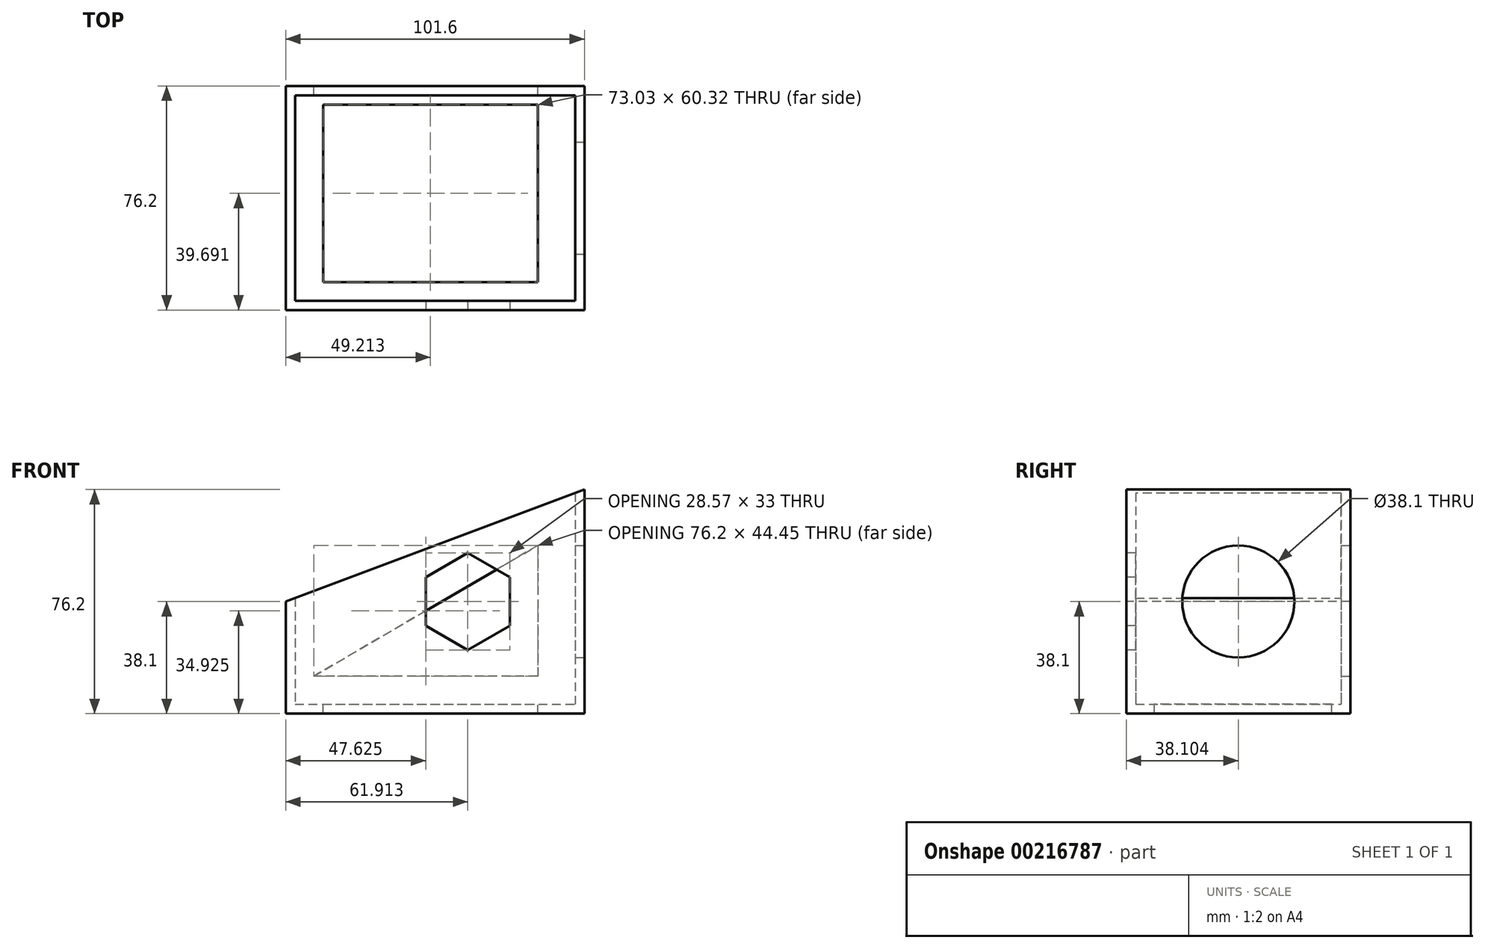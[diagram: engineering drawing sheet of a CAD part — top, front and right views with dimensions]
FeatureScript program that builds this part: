
annotation { "Feature Type Name" : "Feature", "Feature Type Description" : "" }
export const myFeature = defineFeature(function(context is Context, id is Id, definition is map)
    precondition{}
    {
        {
            var Q0;
            Q0=qCreatedBy(makeId("Top.planeOp"),FACE);
            var sketch = newSketch(context, id + "F0", { "sketchPlane" : qUnion([Q0])});
            skLineSegment(sketch, "E0.bottom", {"start": v(-48.15, -36.29) * mm, "end": v(53.45, -36.29) * mm});
            skLineSegment(sketch, "E0.top", {"start": v(-48.15, 39.91) * mm, "end": v(53.45, 39.91) * mm});
            skLineSegment(sketch, "E0.left", {"start": v(-48.15, -36.29) * mm, "end": v(-48.15, 39.91) * mm});
            skLineSegment(sketch, "E0.right", {"start": v(53.45, -36.29) * mm, "end": v(53.45, 39.91) * mm});
            skSolve(sketch);
        }
        {
            var Q0;
            Q0=makeQuery(id+"F0.imprint","IMPRINT",FACE,{"disambiguationData":[TD([[makeQuery(id+"F0.imprint","IMPRINT",EDGE,{"derivedFrom":sQuery(id+"F0.wireOp",EDGE,"E0.bottom")}),1.0]])]});
            extrude(context, id + "F1", {"entities" : qUnion([Q0]), "depth" : 3.17 * mm});
        }
        {
            var Q0;
            Q0=makeQuery(id+"F1.opExtrude","CAP_FACE",FACE,{"disambiguationData":[OSD([sQuery(id+"F0.wireOp",EDGE,"E0.bottom"),sQuery(id+"F0.wireOp",EDGE,"E0.top"),sQuery(id+"F0.wireOp",EDGE,"E0.left"),sQuery(id+"F0.wireOp",EDGE,"E0.right")])],"isStart":false});
            var sketch = newSketch(context, id + "F2", { "sketchPlane" : qUnion([Q0])});
            skLineSegment(sketch, "E1.bottom", {"start": v(-48.15, -36.29) * mm, "end": v(53.45, -36.29) * mm});
            skLineSegment(sketch, "E1.top", {"start": v(-48.15, 39.91) * mm, "end": v(53.45, 39.91) * mm});
            skLineSegment(sketch, "E1.left", {"start": v(-48.15, -36.29) * mm, "end": v(-48.15, 39.91) * mm});
            skLineSegment(sketch, "E1.right", {"start": v(53.45, -36.29) * mm, "end": v(53.45, 39.91) * mm});
            skLineSegment(sketch, "E2.0", {"start": v(50.28, 36.74) * mm, "end": v(-44.97, 36.74) * mm});
            skLineSegment(sketch, "E2.1", {"start": v(50.28, -33.11) * mm, "end": v(50.28, 36.74) * mm});
            skLineSegment(sketch, "E2.2", {"start": v(-44.97, -33.11) * mm, "end": v(50.28, -33.11) * mm});
            skLineSegment(sketch, "E2.3", {"start": v(-44.97, 36.74) * mm, "end": v(-44.97, -33.11) * mm});
            skSolve(sketch);
        }
        {
            var Q0;
            Q0 = qSketchRegion(id + "F2", true);
            extrude(context, id + "F3", {"entities" : qUnion([Q0]), "operationType" : NewBodyOperationType.ADD, "depth" : 73.02 * mm});
        }
        {
            var Q0;
            Q0=makeQuery(id+"F3.boolean.opBoolean","MERGE",FACE,{"derivedFrom":[makeQuery(id+"F1.opExtrude","SWEPT_FACE",FACE,{"disambiguationData":[OSD([sQuery(id+"F0.wireOp",EDGE,"E0.bottom")])]}),makeQuery(id+"F3.opExtrude","SWEPT_FACE",FACE,{"disambiguationData":[OSD([sQuery(id+"F2.wireOp",EDGE,"E1.bottom")])]})]});
            var sketch = newSketch(context, id + "F4", { "sketchPlane" : qUnion([Q0])});
            skLineSegment(sketch, "E3", {"start": v(-48.15, 0) * mm, "end": v(-48.15, 38.1) * mm, "construction": true});
            skLineSegment(sketch, "E4", {"start": v(-48.15, 38.1) * mm, "end": v(53.45, 76.2) * mm});
            skLineSegment(sketch, "E5", {"start": v(-48.15, 38.1) * mm, "end": v(-48.15, 76.2) * mm});
            skLineSegment(sketch, "E6", {"start": v(-48.15, 76.2) * mm, "end": v(53.45, 76.2) * mm});
            skSolve(sketch);
        }
        {
            var Q0;
            Q0 = qSketchRegion(id + "F4", true);
            extrude(context, id + "F5", {"entities" : qUnion([Q0]), "operationType" : NewBodyOperationType.REMOVE, "endBound" : BoundingType.THROUGH_ALL, "oppositeDirection" : true, "depth" : 25.4 * mm});
        }
        {
            var Q0;
            Q0=makeQuery(id+"F3.boolean.opBoolean","MERGE",FACE,{"derivedFrom":[makeQuery(id+"F1.opExtrude","SWEPT_FACE",FACE,{"disambiguationData":[OSD([sQuery(id+"F0.wireOp",EDGE,"E0.right")])]}),makeQuery(id+"F3.opExtrude","SWEPT_FACE",FACE,{"disambiguationData":[OSD([sQuery(id+"F2.wireOp",EDGE,"E1.right")])]})]});
            var sketch = newSketch(context, id + "F6", { "sketchPlane" : qUnion([Q0])});
            skCircle(sketch, "E7", {"center": v(1.81, 38.1) * mm, "radius": 19.05 * mm});
            skPoint(sketch, "E7.centerSnap0", {"position": v(39.91, 38.1) * mm});
            skPoint(sketch, "E7.centerSnap1", {"position": v(1.81, 76.2) * mm});
            skSolve(sketch);
        }
        {
            var Q0;
            Q0 = qSketchRegion(id + "F6", true);
            extrude(context, id + "F7", {"entities" : qUnion([Q0]), "operationType" : NewBodyOperationType.REMOVE, "oppositeDirection" : true, "depth" : 25.4 * mm});
        }
        {
            var Q0;
            Q0=makeQuery(id+"F1.opExtrude","CAP_FACE",FACE,{"disambiguationData":[OSD([sQuery(id+"F0.wireOp",EDGE,"E0.bottom"),sQuery(id+"F0.wireOp",EDGE,"E0.top"),sQuery(id+"F0.wireOp",EDGE,"E0.left"),sQuery(id+"F0.wireOp",EDGE,"E0.right")])],"isStart":false});
            var sketch = newSketch(context, id + "F8", { "sketchPlane" : qUnion([Q0])});
            skLineSegment(sketch, "E8.bottom", {"start": v(-35.45, 33.56) * mm, "end": v(37.58, 33.56) * mm});
            skLineSegment(sketch, "E8.top", {"start": v(-35.45, -26.76) * mm, "end": v(37.58, -26.76) * mm});
            skLineSegment(sketch, "E8.left", {"start": v(-35.45, 33.56) * mm, "end": v(-35.45, -26.76) * mm});
            skLineSegment(sketch, "E8.right", {"start": v(37.58, 33.56) * mm, "end": v(37.58, -26.76) * mm});
            skSolve(sketch);
        }
        {
            var Q0;
            Q0 = qSketchRegion(id + "F8", true);
            extrude(context, id + "F9", {"entities" : qUnion([Q0]), "operationType" : NewBodyOperationType.REMOVE, "endBound" : BoundingType.THROUGH_ALL, "oppositeDirection" : true, "depth" : 25.4 * mm});
        }
        {
            var Q0;
            Q0=makeQuery(id+"F3.boolean.opBoolean","MERGE",FACE,{"derivedFrom":[makeQuery(id+"F1.opExtrude","SWEPT_FACE",FACE,{"disambiguationData":[OSD([sQuery(id+"F0.wireOp",EDGE,"E0.bottom")])]}),makeQuery(id+"F3.opExtrude","SWEPT_FACE",FACE,{"disambiguationData":[OSD([sQuery(id+"F2.wireOp",EDGE,"E1.bottom")])]})]});
            var sketch = newSketch(context, id + "F10", { "sketchPlane" : qUnion([Q0])});
            skCircle(sketch, "E9.cCircle", {"center": v(13.76, 38.1) * mm, "radius": 14.29 * mm, "construction": true});
            skLineSegment(sketch, "E9.0", {"start": v(28.05, 46.35) * mm, "end": v(28.05, 29.85) * mm});
            skLineSegment(sketch, "E9.1", {"start": v(28.05, 29.85) * mm, "end": v(13.76, 21.6) * mm});
            skLineSegment(sketch, "E9.2", {"start": v(13.76, 21.6) * mm, "end": v(-0.52, 29.85) * mm});
            skLineSegment(sketch, "E9.3", {"start": v(-0.52, 29.85) * mm, "end": v(-0.52, 46.35) * mm});
            skLineSegment(sketch, "E9.4", {"start": v(-0.52, 46.35) * mm, "end": v(13.76, 54.6) * mm});
            skLineSegment(sketch, "E9.5", {"start": v(13.76, 54.6) * mm, "end": v(28.05, 46.35) * mm});
            skPoint(sketch, "E9.0.midPoint", {"position": v(28.05, 38.1) * mm});
            skPoint(sketch, "E10", {"position": v(53.45, 38.1) * mm});
            skSolve(sketch);
        }
        {
            var Q0;
            Q0 = qSketchRegion(id + "F10", true);
            extrude(context, id + "F11", {"entities" : qUnion([Q0]), "operationType" : NewBodyOperationType.REMOVE, "oppositeDirection" : true, "depth" : 25.4 * mm});
        }
        {
            var Q0;
            Q0=makeQuery(id+"F3.boolean.opBoolean","MERGE",FACE,{"derivedFrom":[makeQuery(id+"F1.opExtrude","SWEPT_FACE",FACE,{"disambiguationData":[OSD([sQuery(id+"F0.wireOp",EDGE,"E0.top")])]}),makeQuery(id+"F3.opExtrude","SWEPT_FACE",FACE,{"disambiguationData":[OSD([sQuery(id+"F2.wireOp",EDGE,"E1.top")])]})]});
            var sketch = newSketch(context, id + "F12", { "sketchPlane" : qUnion([Q0])});
            skLineSegment(sketch, "E11", {"start": v(-37.58, 57.15) * mm, "end": v(-37.58, 12.7) * mm});
            skLineSegment(sketch, "E12", {"start": v(-37.58, 12.7) * mm, "end": v(38.62, 12.7) * mm});
            skLineSegment(sketch, "E13", {"start": v(38.62, 12.7) * mm, "end": v(-37.58, 57.15) * mm});
            skSolve(sketch);
        }
        {
            var Q0;
            Q0 = qSketchRegion(id + "F12", true);
            extrude(context, id + "F13", {"entities" : qUnion([Q0]), "operationType" : NewBodyOperationType.REMOVE, "oppositeDirection" : true, "depth" : 25.4 * mm});
        }
    });
